# Revit family: Haworth_Masters_FreestandingLateral_3High4High
name_source: partatom
category: Furniture Systems
revit_build: Autodesk Revit 2018 (Build: 20170223_1515(x64)
units: mm (PartAtom-declared; Revit-internal decimal feet)

## family parameters
Always vertical = Yes
Cut with Voids When Loaded = No
OmniClass Number = 23.40.70.14.64.21
OmniClass Title = Systems Furniture
Part Type = Normal
Room Calculation Point = No
Round Connector Dimension = Use Diameter
Shared = No
Work Plane-Based = No

## types (8) — shared parameters
Assembly Code = E2020200
Bar Pull = Yes
Bar Pull Length = 24"
Base Height = 2 9/16"
Bottom Cabinet Height = 15 25/64"
Classic Pull = No
Classic Pull Length = 8"
Custom Size = No
Drawer 1 Height = 12 9/16"
Drawer 2 Height = 12 9/16"
Drawer 4 Height = 13 15/32"
Finger Pull = No
Leg Offset = 0"
Linear Pull = No
Manufacturer = Haworth
Max. Depth = 24"
Max. Height = 55 5/16"
Max. Width = 36"
Min. Depth = 19"
Min. Height = 41 5/8"
Min. Width = 30"
Model = Haworth Masters
Revision Number = 1
Standard Depths = 19, 24 in.
Standard Heights = 41 5/8, 55 5/16 in.
Standard Widths = 30, 36 in.
Sustainability Info = https://www.haworth.com
Top Thickness = 3/4"
URL = http://www.haworth.com
Verify Final Dim. w/ Haworth = Verify Final Dim. w/ Haworth
Warranty = http://www.haworth.com

## per-type parameters (varying)
| type | Actual Depth | Actual Height | Actual Width | Depth | Description | Drawer 3 Height | Drawer Width | Four High | Shelf Depth | Shelf Width | Three High | Top Drawer Offset | URL - Product | Width |
| 19d 30w 41h | 19" | 41 5/8" | 30" | 19" | Haworth Masters - Freestanding Lateral File - 3High - 19d 30w | 13 15/32" | 30" | No | 17 1/2" | 28 1/2" | Yes | 0" | http://www.haworth.com | 30" |
| 19d 36w 41h | 19" | 41 5/8" | 36" | 19" | Haworth Masters - Freestanding Lateral File - 3High - 19d 36w | 13 15/32" | 36" | No | 17 1/2" | 34 1/2" | Yes | 0" | http://www.haworth.com | 36" |
| 24d 36w 41h | 24" | 41 5/8" | 36" | 24" | Haworth Masters - Freestanding Lateral File - 3High - 24d 36w | 13 15/32" | 36" | No | 22 1/2" | 34 1/2" | Yes | 0" | http://www.haworth.com | 36" |
| 24d 30w 41h | 24" | 41 5/8" | 30" | 24" | Haworth Masters - Freestanding Lateral File - 3High - 24d 30w | 13 15/32" | 30" | No | 22 1/2" | 28 1/2" | Yes | 0" | http://www.haworth.com | 30" |
| 19d 36w 55h | 19" | 55 5/16" | 36" | 19" | Haworth Masters - Freestanding Lateral File - 4High - 19d 36w | 13 1/2" | 36" | Yes | 17 1/2" | 34 1/2" | No | 13 5/8" | http://www.haworth.com | 36" |
| 19d 30w 55h | 19" | 55 5/16" | 30" | 19" | Haworth Masters - Freestanding Lateral File - 4High - 19d 30w | 13 1/2" | 30" | Yes | 17 1/2" | 28 1/2" | No | 13 5/8" | http://www.haworth.com | 30" |
| 24d 30w 55h | 24" | 55 5/16" | 30" | 24" | Haworth Masters - Freestanding Lateral File - 4High - 24d 30w | 13 1/2" | 30" | Yes | 22 1/2" | 28 1/2" | No | 13 5/8" | http://www.haworth.com | 30" |
| 24d 36w 55h | 24" | 55 5/16" | 36" | 24" | Haworth Masters - Freestanding Lateral File - 4High - 24d 36w | 13 1/2" | 36" | Yes | 22 1/2" | 34 1/2" | No | 13 5/8" | https://www.haworth.com | 36" |

## geometry (parser evidence)
native form markers: Sweep x6
no freeform markers — native parametric forms only
